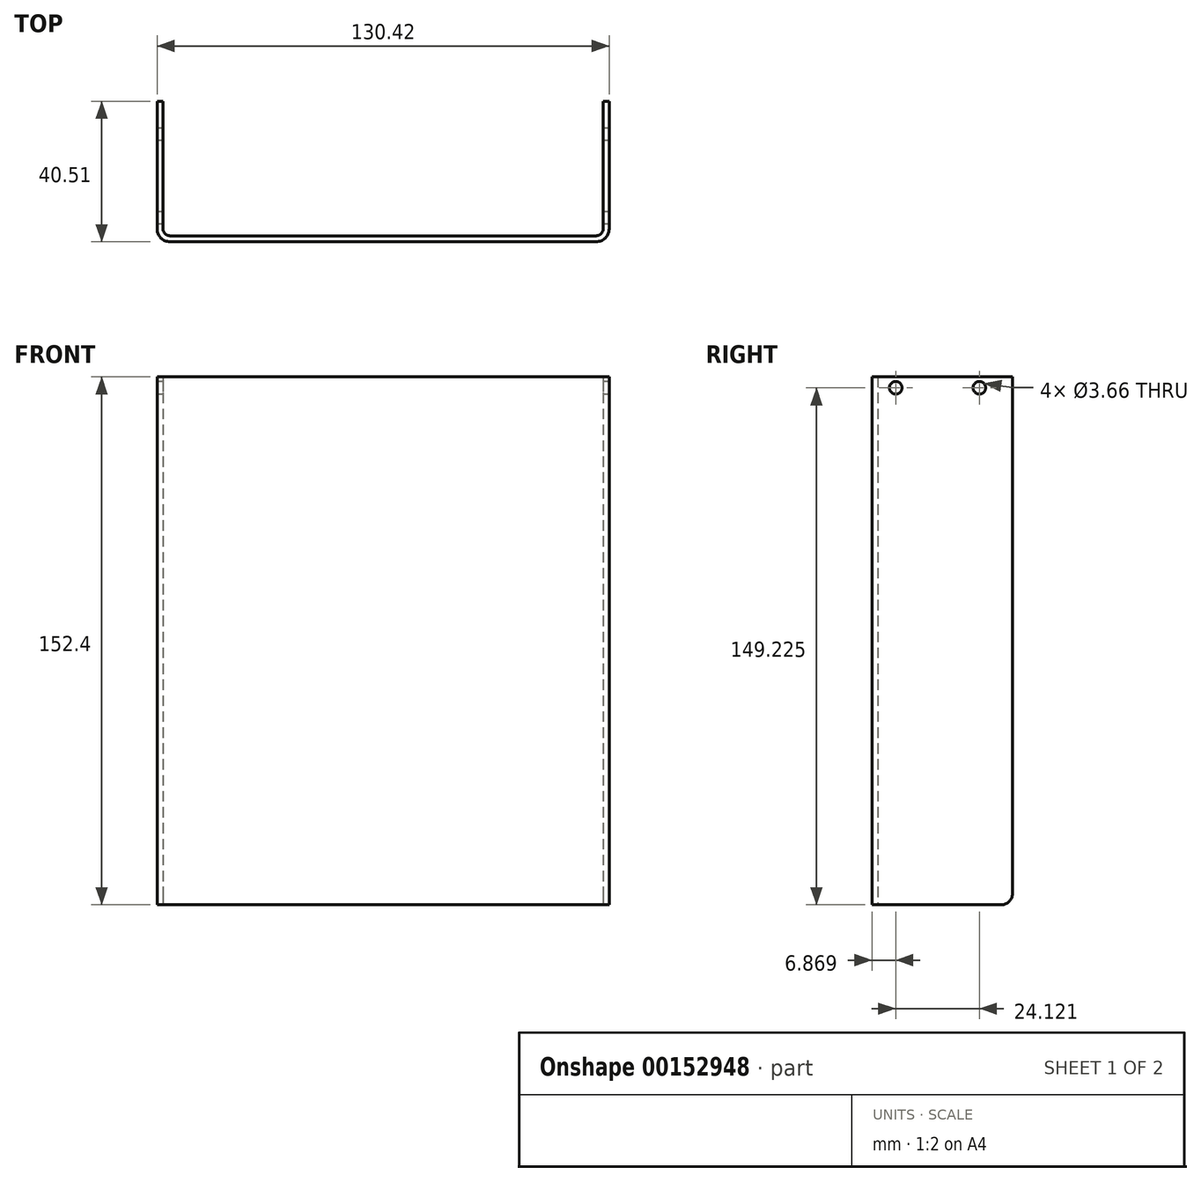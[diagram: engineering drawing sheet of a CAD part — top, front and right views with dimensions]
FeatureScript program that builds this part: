
annotation { "Feature Type Name" : "Feature", "Feature Type Description" : "" }
export const myFeature = defineFeature(function(context is Context, id is Id, definition is map)
    precondition{}
    {
        {
            var Q0;
            Q0=qCreatedBy(makeId("Top.planeOp"),FACE);
            var sketch = newSketch(context, id + "F0", { "sketchPlane" : qUnion([Q0])});
            skLineSegment(sketch, "E0.bottom", {"start": v(0, 0) * mm, "end": v(-127, 0) * mm});
            skLineSegment(sketch, "E0.top", {"start": v(1.7, -1.7) * mm, "end": v(-128.7, -1.7) * mm});
            skLineSegment(sketch, "E1.top", {"start": v(-127, 38.8) * mm, "end": v(-128.7, 38.8) * mm});
            skLineSegment(sketch, "E1.left", {"start": v(-127, 0) * mm, "end": v(-127, 38.8) * mm});
            skLineSegment(sketch, "E1.right", {"start": v(-128.7, -1.7) * mm, "end": v(-128.7, 38.8) * mm});
            skLineSegment(sketch, "E2.top", {"start": v(0, 38.8) * mm, "end": v(1.7, 38.8) * mm});
            skLineSegment(sketch, "E2.left", {"start": v(0, 0) * mm, "end": v(0, 38.8) * mm});
            skLineSegment(sketch, "E2.right", {"start": v(1.7, -1.7) * mm, "end": v(1.7, 38.8) * mm});
            skLineSegment(sketch, "E3", {"start": v(-63.5, 0) * mm, "end": v(-63.5, -1.7) * mm, "construction": true});
            skSolve(sketch);
        }
        {
            var Q0;
            Q0=qSketchRegion(id+"F0",true);
            extrude(context, id + "F1", {"entities" : qUnion([Q0]), "depth" : 152.4 * mm});
        }
        {
            var Q0;
            Q0=makeQuery(id+"FcdIcV9w6YY9zah_1.opExtrude","CAP_EDGE",EDGE,{"disambiguationData":[OSD([sQuery(id+"FU7sgaIbCbRhSfr_1.wireOp",EDGE,"F29Sxc5V-O2cl-wjtz-gx5o-reTTBG7m1pNU.top")])],"isStart":true});
            var Q1;
            Q1=makeQuery(id+"FcdIcV9w6YY9zah_1.opExtrude","CAP_EDGE",EDGE,{"disambiguationData":[OSD([sQuery(id+"FU7sgaIbCbRhSfr_1.wireOp",EDGE,"yv2bQU74-Eht6-uYuo-WBF2-3C4kyuaz0slr.top")])],"isStart":true});
            var Q2;
            Q2=makeQuery(id+"F1.opExtrude","SWEPT_EDGE",EDGE,{"disambiguationData":[OSD([sQuery(id+"F0.wireOp",EDGE,"E0.bottom"),sQuery(id+"F0.wireOp",EDGE,"E2.left")])]});
            var Q3;
            Q3=makeQuery(id+"F1.opExtrude","SWEPT_EDGE",EDGE,{"disambiguationData":[OSD([sQuery(id+"F0.wireOp",EDGE,"E0.bottom"),sQuery(id+"F0.wireOp",EDGE,"E1.left")])]});
            fillet(context, id + "F2", {"entities" : qUnion([Q0, Q1, Q2, Q3]), "radius" : 1.98 * mm, "tangentPropagation" : true, "allowEdgeOverflow" : false});
        }
        {
            var Q0;
            Q0=makeQuery(id+"FkwQQH4eT4IjhdK_1.opExtrude","CAP_EDGE",EDGE,{"disambiguationData":[OSD([sQuery(id+"FvDFSbhwMPyTNrQ_1.wireOp",EDGE,"223FG13h-YrEq-unoX-9EOi-DwKLLmwbrteD.top")])],"isStart":false});
            var Q1;
            Q1=makeQuery(id+"F1.opExtrude","SWEPT_EDGE",EDGE,{"disambiguationData":[OSD([sQuery(id+"F0.wireOp",EDGE,"E0.top"),sQuery(id+"F0.wireOp",EDGE,"E2.right")])]});
            var Q2;
            Q2=makeQuery(id+"F1.opExtrude","SWEPT_EDGE",EDGE,{"disambiguationData":[OSD([sQuery(id+"F0.wireOp",EDGE,"E0.top"),sQuery(id+"F0.wireOp",EDGE,"E1.right")])]});
            var Q3;
            Q3=makeQuery(id+"F2kHonbXZaQoFrR_1.opExtrude","CAP_EDGE",EDGE,{"disambiguationData":[OSD([sQuery(id+"FsAbJG8AZOSwdHE_1.wireOp",EDGE,"WRaIy3id-o2EU-qHqw-IwdC-eHQZRSiK4KpF.bottom")])],"isStart":false});
            fillet(context, id + "F3", {"entities" : qUnion([Q0, Q1, Q2, Q3]), "radius" : 3.7 * mm, "tangentPropagation" : true, "allowEdgeOverflow" : false});
        }
        {
            var Q0;
            Q0=makeQuery(id+"F1.opExtrude","SWEPT_FACE",FACE,{"disambiguationData":[OSD([sQuery(id+"F0.wireOp",EDGE,"E1.right")])]});
            var sketch = newSketch(context, id + "F4", { "sketchPlane" : qUnion([Q0])});
            skLineSegment(sketch, "E4", {"start": v(-38.8, 149.22) * mm, "end": v(-29.28, 149.22) * mm, "construction": true});
            skLineSegment(sketch, "E5", {"start": v(-29.28, 149.22) * mm, "end": v(-5.16, 149.22) * mm, "construction": true});
            skLineSegment(sketch, "E6", {"start": v(-5.16, 149.22) * mm, "end": v(-1.98, 149.22) * mm, "construction": true});
            skCircle(sketch, "E7", {"center": v(-29.28, 149.22) * mm, "radius": 1.83 * mm});
            skCircle(sketch, "E8", {"center": v(-5.16, 149.22) * mm, "radius": 1.83 * mm});
            skLineSegment(sketch, "E9", {"start": v(-5.16, 149.22) * mm, "end": v(-5.16, 152.4) * mm, "construction": true});
            skSolve(sketch);
        }
        {
            var Q0;
            Q0 = qSketchRegion(id + "F4", true);
            var Q1;
            Q1=makeQuery(id+"F1.opExtrude","SWEPT_FACE",FACE,{"disambiguationData":[OSD([sQuery(id+"F0.wireOp",EDGE,"E2.right")])]});
            extrude(context, id + "F5", {"entities" : qUnion([Q0]), "operationType" : NewBodyOperationType.REMOVE, "endBound" : BoundingType.UP_TO_SURFACE, "oppositeDirection" : true, "endBoundEntityFace" : qUnion([Q1]), "depth" : 25.4 * mm});
        }
        {
            var Q0;
            Q0=makeQuery(id+"F1.opExtrude","CAP_EDGE",EDGE,{"disambiguationData":[OSD([sQuery(id+"F0.wireOp",EDGE,"E2.top")])],"isStart":true});
            var Q1;
            Q1=makeQuery(id+"F1.opExtrude","CAP_EDGE",EDGE,{"disambiguationData":[OSD([sQuery(id+"F0.wireOp",EDGE,"E1.top")])],"isStart":true});
            fillet(context, id + "F6", {"entities" : qUnion([Q0, Q1]), "radius" : 3.17 * mm, "tangentPropagation" : true, "allowEdgeOverflow" : false});
        }
    });
